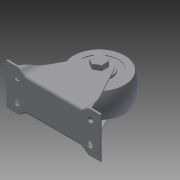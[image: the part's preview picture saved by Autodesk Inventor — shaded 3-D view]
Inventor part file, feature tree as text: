
AUTODESK INVENTOR PART (.ipt)
format: ipt  version: 2014 (Build 180170000, 170)  size: 369,152 bytes
history: native  units: in
note: dims shown in document units (in); Inventor stores cm internally (conversion verified against a paired STEP export)
features: imported_body x2, revolve x1, other x1, boolean_combine x1
ambient origin geometry x8: Origin, YZ Plane, XZ Plane, XY Plane, X Axis, Y Axis, Z Axis, Center Point
bodies: Body1 (feature_tree), Body2 (feature_tree)
feature tree (5):
  revolve  "Revolve1"  [1 undecoded]
  other  "2457T460_CART-SMART CASTER1"
  boolean_combine  "Combine1"
  imported_body  "Base1"
  imported_body  "Base2"
note: 1 required parameter value undecoded (feature->parameter linkage not recoverable at this tier; creation-order binding heuristic only, values carry confidence <= 0.55)
